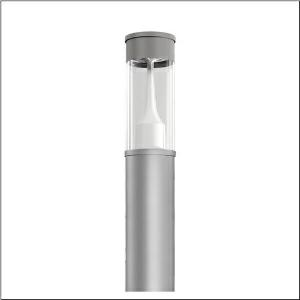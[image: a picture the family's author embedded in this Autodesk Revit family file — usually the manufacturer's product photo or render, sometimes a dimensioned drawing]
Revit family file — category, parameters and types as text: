
# Revit family: city-light_400_iq___p1_0a_5xa5305lf14hp_1a81
name_source: partatom
category: Lighting Fixtures
units: mm (PartAtom-declared; Revit-internal decimal feet)

## family parameters
Cut with Voids When Loaded = No
Host = Face
Light Source = No
Part Type = Normal
Room Calculation Point = No
Round Connector Dimension = Use Diameter
Shared = No

## types (1)
- --- (1 x LED, 4910 lm, 33.6 W, 4000K)
    Apparent Load = 34 VA
    CIE Flux Codes = 31 62 91 95 100
    Color Rendering = 70
    Color Temperature = 4000K
    Default Elevation = 1800 mm
    Description = City-Light 400 iQ, light pillar, Module 540 iQ-SR, primary light control with 3 zone facetted reflector, of plastic, silver coated, highly specular, structured, primary optical cover: cover, of PMMA, transparent, partly coated, light distribution: P1.0a, primary light characteristic: strongly asymmetric, LED, High Power LED, rated luminous flux: 4.910lm, luminous efficacy: 146lm/W, light colour: 740, colour temperature: 4000K, control gear: ECG iQ, control: presetting dimming logarithmic, Street-Remote, Auto-Match, Temp-Guard, Lumen-Switch, Night-Set, Smart-Wire, Light-Fading, Desk-Remote (wireless, voltage-free reading and setting of iQ features in the workshop via application-optimized NFC function/RFID function), optimised constant luminous flux control (CLO 2.0), with terminal, 6-pole, max. 2.5mm², mains connection: 230..240V, AC, 50/60Hz, start of lifetime: 34W, end of service life: 36W, reduction: 15W, luminaire housing, cylindrical, of extruded aluminium section, coated, Siteco® metallic grey (DB 702S), length: 4.694mm, diameter: 200mm, Module 540 iQ-SR, traffic white (RAL 9016), equipment: Power, protection rating (complete): IP65, insulation class (complete): insulation class II (safety insulation), certification: CE, ENEC, VDE, packaging unit: 1 piece

Light Distribution: P1.0a
    Height = 500 mm
    Lamp = 1 x LED
    Lamp Light Flux = 4910 lm
    Lamp Power = 33.6 W
    Lamp count = 1
    Length = 200 mm  [stored 0.656168 ft]
    Luminous efficacy = 146 lm/W
    Manufacturer = Siteco
    ModVariant = No
    Model = 5XA5305LF14HP
    Mounting Place = Floor
    Mounting Type = Freestanding
    Number of Poles = 1
    OnlyDefault = Yes
    Power Factor = 1
    Product Name = City-Light 400 iQ | P1.0a
    Product group = light pillar
    ProductGroupID = 1303
    Protection Class = Protection class II
    Protection Degree = IP 65
    RLX_Detail_Level = 1
    RLX_Emergency_Light_Flux = 0 lm
    RLX_Emergency_Type = 0
    RLX_Emergency_Type_DB = No
    RlxData = <blob elided: 53417 chars, md5=27b5ab6d>
    Socket = socket
    Standby Power = 0 W
    System Light Flux = 4910 lm
    System Power = 34 W
    Type Comments = factory setting: luminous flux: 100 % | dim-lin: 254 | 695 mA
    Type Image = l_1006916.jpg
    URL = http://relux.com
    VarID = @adj_145353
    Voltage = 0 V
    Weight = 0.00 kg
    Width = 0 mm  [stored 0 ft]

note: [stored X ft] marks values corroborated as IEEE doubles in the binary element streams (Revit-internal decimal feet)

## geometry (parser evidence)
native form markers: Blend x4, Sweep x11
no freeform markers — native parametric forms only
